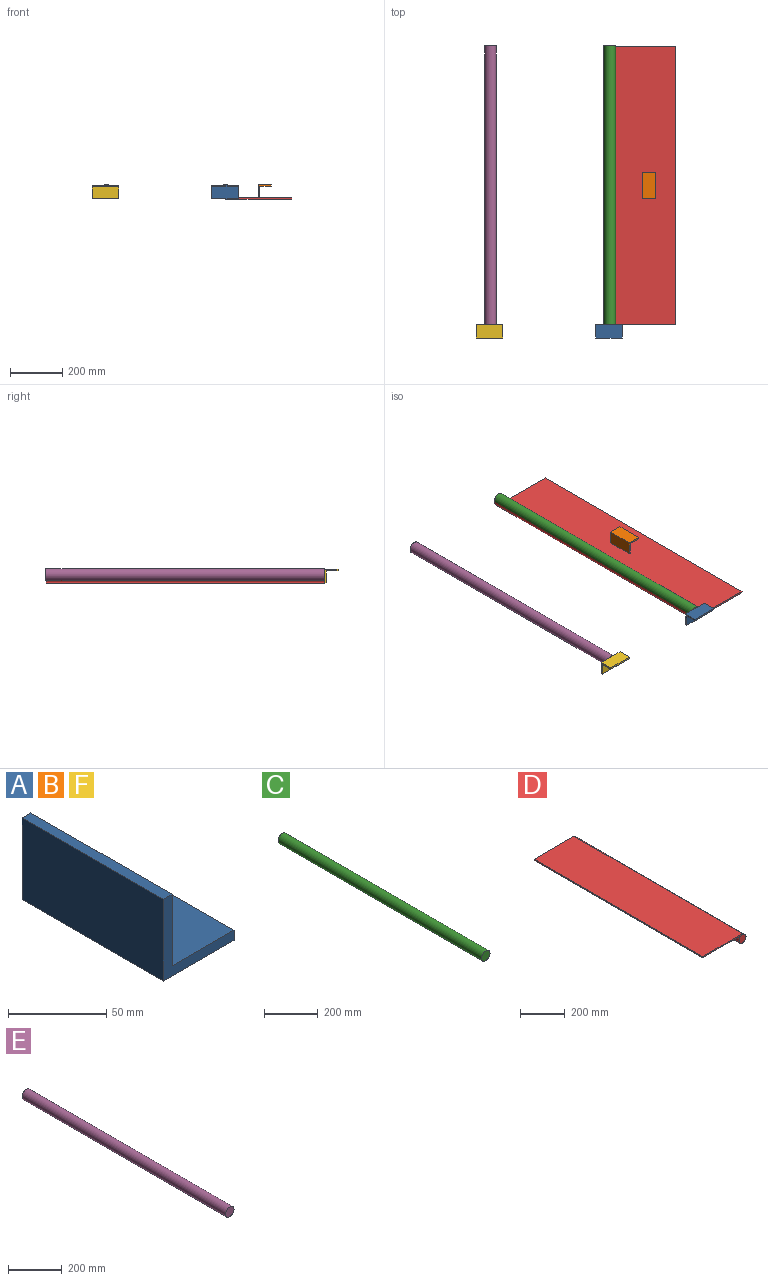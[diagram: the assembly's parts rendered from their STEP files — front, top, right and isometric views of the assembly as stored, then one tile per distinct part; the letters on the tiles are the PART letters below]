
ASSEMBLY  parts=6 mates=3
PART A: 8 faces, bbox 50.8x101.6x50.8 mm
  f0: plane 50.8x50.8mm, normal (0,-1,0), area 604.8mm2, adj f1,f3,f4,f5,f6,f7
  f1: plane 101.6x50.8mm, normal (0,0,-1), area 5161.3mm2, adj f0,f2,f5,f6
  f2: plane 50.8x50.8mm, normal (0,1,0), area 604.8mm2, adj f1,f3,f4,f5,f6,f7
  f3: plane 101.6x6.35mm, normal (0,0,1), area 645.2mm2, adj f0,f2,f4,f5
  f4: plane 101.6x44.45mm, normal (1,0,0), area 4516.1mm2, adj f0,f2,f3,f7
  f5: plane 101.6x50.8mm, normal (-1,0,0), area 5161.3mm2, adj f0,f1,f2,f3
  f6: plane 101.6x6.35mm, normal (1,0,0), area 645.2mm2, adj f0,f1,f2,f7
  f7: plane 101.6x44.45mm, normal (0,0,1), area 4516.1mm2, adj f0,f2,f4,f6
PART B: same geometry as A
PART C: 3 faces, bbox 44.5x1066.8x44.5 mm
  f0: cylinder r=22.23mm len=1066.8mm, axis (0,-1,0), area 148972mm2, adj f1,f2
  f1: plane 44.45x44.45mm, normal (0,1,0), area 1551.8mm2, adj f0
  f2: plane 44.45x44.45mm, normal (0,-1,0), area 1551.8mm2, adj f0
PART D: 7 faces, bbox 274.4x1066.8x50.7 mm
  f0: cylinder r=22.23mm len=1066.8mm, axis (0,-1,0), area 147071.6mm2, adj f1,f2,f4,f6
  f1: plane 274.45x50.73mm, normal (0,1,0), area 3153.3mm2, adj f0,f3,f4,f5,f6
  f2: plane 274.45x50.73mm, normal (0,-1,0), area 3153.3mm2, adj f0,f3,f4,f5,f6
  f3: plane 1066.8x6.35mm, normal (-1,0,0), area 6774.2mm2, adj f1,f2,f5,f6
  f4: plane 1066.8x6.28mm, normal (1,0,0), area 6698.1mm2, adj f0,f1,f2,f5
  f5: plane 1066.8x252.22mm, normal (0,0,1), area 269068.8mm2, adj f1,f2,f3,f4
  f6: plane 1066.8x250.44mm, normal (0,0,-1), area 267170.4mm2, adj f0,f1,f2,f3
PART E: 3 faces, bbox 44.5x1066.8x44.5 mm
  f0: cylinder r=22.23mm len=1066.8mm, axis (0,-1,0), area 148972mm2, adj f1,f2
  f1: plane 44.45x44.45mm, normal (0,1,0), area 1551.8mm2, adj f0
  f2: plane 44.45x44.45mm, normal (0,-1,0), area 1551.8mm2, adj f0
PART F: same geometry as A
PLACE A rot(axis=(-0.71,0.71,0),180deg) t=(508,0,25.4)mm
PLACE B rot(axis=(0,1,0),90.2deg) t=(584.11,483.18,28.31)mm
PLACE C t=(2.83,1.85,5.65)mm
PLACE D rot(axis=(0,-1,0),179.8deg) t=(1171.4,0.58,-2.13)mm
PLACE E t=(2.83,1.85,5.65)mm
PLACE F rot(axis=(-0.71,0.71,0),180deg) t=(50.8,0,25.4)mm
MATE parallel A.f5 <-> C.f0  axis (0,1,0) through (457.2,0,0)mm
MATE parallel F.f5 <-> E.f0  axis (0,1,0) through (0,0,0)mm
MATE parallel B.f6 <-> D.f6  axis (0,0,-1) through (587.13,533.98,-22.5)mm
